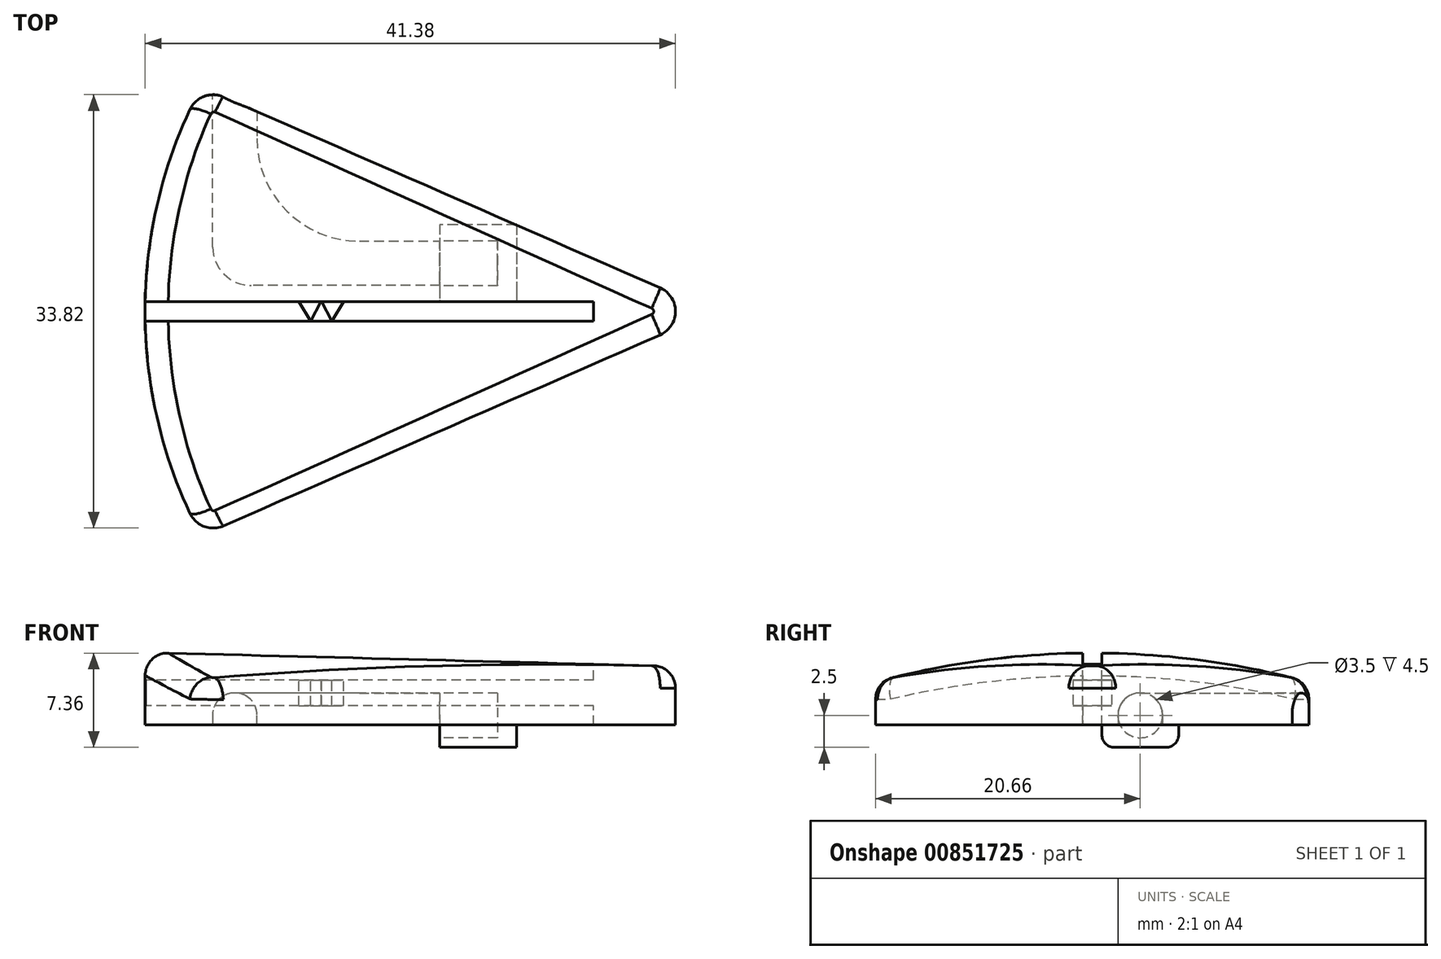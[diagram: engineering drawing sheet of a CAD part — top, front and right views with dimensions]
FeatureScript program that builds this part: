
annotation { "Feature Type Name" : "Feature", "Feature Type Description" : "" }
export const myFeature = defineFeature(function(context is Context, id is Id, definition is map)
    precondition{}
    {
        {
            var Q0;
            Q0=qCreatedBy(makeId("Top.planeOp"),FACE);
            var sketch = newSketch(context, id + "F0", { "sketchPlane" : qUnion([Q0])});
            skLineSegment(sketch, "E0", {"start": v(0, 0) * mm, "end": v(-40, 17.5) * mm, "construction": true});
            skLineSegment(sketch, "E1", {"start": v(-40, 17.5) * mm, "end": v(-40, -17.5) * mm, "construction": true});
            skLineSegment(sketch, "E2", {"start": v(-40, -17.5) * mm, "end": v(0, 0) * mm, "construction": true});
            skLineSegment(sketch, "E3", {"start": v(-4.19, 1.83) * mm, "end": v(-38.26, 16.74) * mm});
            skLineSegment(sketch, "E4", {"start": v(-38.26, -16.74) * mm, "end": v(-4.19, -1.83) * mm});
            skPoint(sketch, "E5.visualSharp", {"position": v(0, 0) * mm});
            skArc(sketch, "E5.filletArc", {"start": v(-4.19, -1.83) * mm, "mid": v(-2.99, 0) * mm, "end": v(-4.19, 1.83) * mm});
            skArc(sketch, "E6", {"start": v(-40.87, 15.75) * mm, "mid": v(-44.37, 0) * mm, "end": v(-40.87, -15.75) * mm});
            skPoint(sketch, "E7.visualSharp", {"position": v(-40, 17.5) * mm});
            skArc(sketch, "E7.filletArc", {"start": v(-38.26, 16.74) * mm, "mid": v(-39.77, 16.78) * mm, "end": v(-40.87, 15.75) * mm});
            skPoint(sketch, "E8.visualSharp", {"position": v(-40, -17.5) * mm});
            skArc(sketch, "E8.filletArc", {"start": v(-40.87, -15.75) * mm, "mid": v(-39.77, -16.78) * mm, "end": v(-38.26, -16.74) * mm});
            skSolve(sketch);
        }
        {
            var Q0;
            Q0 = qSketchRegion(id + "F0", true);
            extrude(context, id + "F1", {"entities" : qUnion([Q0]), "depth" : 6 * mm, "offsetDistance" : 25 * mm});
        }
        {
            var Q0;
            Q0=makeQuery(id+"F1.opExtrude","CAP_FACE",FACE,{"disambiguationData":[OSD([sQuery(id+"F0.wireOp",EDGE,"E3"),sQuery(id+"F0.wireOp",EDGE,"E4"),sQuery(id+"F0.wireOp",EDGE,"E5.filletArc"),sQuery(id+"F0.wireOp",EDGE,"E6"),sQuery(id+"F0.wireOp",EDGE,"E7.filletArc"),sQuery(id+"F0.wireOp",EDGE,"E8.filletArc")])],"isStart":false});
            var sketch = newSketch(context, id + "F2", { "sketchPlane" : qUnion([Q0])});
            skLineSegment(sketch, "E9.bottom", {"start": v(-9.37, 0.75) * mm, "end": v(-44.37, 0.75) * mm});
            skLineSegment(sketch, "E9.top", {"start": v(-9.37, -0.75) * mm, "end": v(-44.37, -0.75) * mm});
            skLineSegment(sketch, "E9.left", {"start": v(-9.37, 0.75) * mm, "end": v(-9.37, -0.75) * mm});
            skLineSegment(sketch, "E9.right", {"start": v(-44.37, 0.75) * mm, "end": v(-44.37, -0.75) * mm});
            skSolve(sketch);
        }
        {
            var Q0;
            Q0 = qSketchRegion(id + "F2", true);
            extrude(context, id + "F3", {"entities" : qUnion([Q0]), "operationType" : NewBodyOperationType.REMOVE, "endBound" : BoundingType.THROUGH_ALL, "oppositeDirection" : true, "depth" : 25 * mm, "offsetDistance" : 25 * mm});
        }
        {
            var Q0;
            Q0=qCreatedBy(makeId("Right.planeOp"),FACE);
            var sketch = newSketch(context, id + "F4", { "sketchPlane" : qUnion([Q0])});
            skLineSegment(sketch, "E10", {"start": v(-18, 2) * mm, "end": v(-18, 0) * mm, "construction": true});
            skLineSegment(sketch, "E11", {"start": v(-18, 0) * mm, "end": v(18, 0) * mm, "construction": true});
            skLineSegment(sketch, "E12", {"start": v(18, 0) * mm, "end": v(18, 2) * mm, "construction": true});
            skArc(sketch, "E13", {"start": v(18, 2) * mm, "mid": v(0, 4.5) * mm, "end": v(-18, 2) * mm});
            skLineSegment(sketch, "E14", {"start": v(-18, 2) * mm, "end": v(-18, 12) * mm});
            skLineSegment(sketch, "E15", {"start": v(-18, 12) * mm, "end": v(18, 12) * mm});
            skLineSegment(sketch, "E16", {"start": v(18, 12) * mm, "end": v(18, 2) * mm});
            skSolve(sketch);
        }
        {
            var Q0;
            Q0 = qSketchRegion(id + "F4", true);
            extrude(context, id + "F5", {"entities" : qUnion([Q0]), "operationType" : NewBodyOperationType.REMOVE, "endBound" : BoundingType.THROUGH_ALL, "oppositeDirection" : true, "depth" : 25 * mm, "offsetDistance" : 25 * mm, "hasDraft" : true, "draftAngle" : 1.5 * degree, "draftPullDirection" : true});
        }
        {
            var Q0;
            {var subQ0=sQuery(id+"F0.wireOp",EDGE,"E8.filletArc");var subQ2=sQuery(id+"F0.wireOp",EDGE,"E6");Q0=makeQuery(id+"F5.boolean.opBoolean","INTERSECT",EDGE,{"derivedFrom":[makeQuery(id+"F3.boolean.opBoolean","SPLIT",FACE,{"disambiguationData":[TD([makeQuery(id+"F1.opExtrude","SWEPT_FACE",FACE,{"disambiguationData":[OSD([subQ0])]})])],"derivedFrom":makeQuery(id+"F1.opExtrude","SWEPT_FACE",FACE,{"disambiguationData":[OSD([subQ2])]})}),makeQuery(id+"F5.opExtrude","SWEPT_FACE",FACE,{"disambiguationData":[OSD([sQuery(id+"F4.wireOp",EDGE,"E13")])]})]});}
            fillet(context, id + "F6", {"entities" : qUnion([Q0]), "radius" : 1.75 * mm, "tangentPropagation" : true, "allowEdgeOverflow" : false});
        }
        {
            var Q0;
            Q0=makeQuery(id+"F1.opExtrude","CAP_FACE",FACE,{"disambiguationData":[OSD([sQuery(id+"F0.wireOp",EDGE,"E3"),sQuery(id+"F0.wireOp",EDGE,"E4"),sQuery(id+"F0.wireOp",EDGE,"E5.filletArc"),sQuery(id+"F0.wireOp",EDGE,"E6"),sQuery(id+"F0.wireOp",EDGE,"E7.filletArc"),sQuery(id+"F0.wireOp",EDGE,"E8.filletArc")])],"isStart":true});
            var sketch = newSketch(context, id + "F7", { "sketchPlane" : qUnion([Q0])});
            skLineSegment(sketch, "E17.bottom", {"start": v(-15.37, -6.75) * mm, "end": v(-21.37, -6.75) * mm});
            skLineSegment(sketch, "E17.top", {"start": v(-15.37, -0.75) * mm, "end": v(-21.37, -0.75) * mm});
            skLineSegment(sketch, "E17.left", {"start": v(-15.37, -6.75) * mm, "end": v(-15.37, -0.75) * mm});
            skLineSegment(sketch, "E17.right", {"start": v(-21.37, -6.75) * mm, "end": v(-21.37, -0.75) * mm});
            skLineSegment(sketch, "E18", {"start": v(-44.18, -3.75) * mm, "end": v(-8.57, -3.75) * mm, "construction": true});
            skPoint(sketch, "E19", {"position": v(-21.37, -3.75) * mm});
            skSolve(sketch);
        }
        {
            var Q0;
            Q0 = qSketchRegion(id + "F7", true);
            extrude(context, id + "F8", {"entities" : qUnion([Q0]), "operationType" : NewBodyOperationType.ADD, "depth" : 1.75 * mm, "offsetDistance" : 25 * mm});
        }
        {
            var Q0;
            Q0=makeQuery(id+"F1.opExtrude","CAP_FACE",FACE,{"disambiguationData":[OSD([sQuery(id+"F0.wireOp",EDGE,"E3"),sQuery(id+"F0.wireOp",EDGE,"E4"),sQuery(id+"F0.wireOp",EDGE,"E5.filletArc"),sQuery(id+"F0.wireOp",EDGE,"E6"),sQuery(id+"F0.wireOp",EDGE,"E7.filletArc"),sQuery(id+"F0.wireOp",EDGE,"E8.filletArc")])],"isStart":true});
            var sketch = newSketch(context, id + "F9", { "sketchPlane" : qUnion([Q0])});
            skLineSegment(sketch, "E20", {"start": v(-21.37, -3.75) * mm, "end": v(-37.37, -3.75) * mm, "construction": true});
            skLineSegment(sketch, "E21", {"start": v(-37.37, -3.75) * mm, "end": v(-37.37, -18.75) * mm, "construction": true});
            skLineSegment(sketch, "E22", {"start": v(-21.37, -2.03) * mm, "end": v(-36.1, -2.03) * mm});
            skLineSegment(sketch, "E23", {"start": v(-39.1, -5.03) * mm, "end": v(-39.1, -18.75) * mm});
            skLineSegment(sketch, "E24", {"start": v(-39.1, -18.75) * mm, "end": v(-35.65, -18.75) * mm});
            skLineSegment(sketch, "E25", {"start": v(-35.65, -18.75) * mm, "end": v(-35.65, -13.48) * mm});
            skLineSegment(sketch, "E26", {"start": v(-27.65, -5.48) * mm, "end": v(-21.37, -5.48) * mm});
            skLineSegment(sketch, "E27", {"start": v(-29.37, -3.75) * mm, "end": v(-29.37, -2.03) * mm, "construction": true});
            skLineSegment(sketch, "E28", {"start": v(-29.37, -3.75) * mm, "end": v(-29.37, -5.48) * mm, "construction": true});
            skLineSegment(sketch, "E29", {"start": v(-37.37, -11.25) * mm, "end": v(-39.1, -11.25) * mm, "construction": true});
            skLineSegment(sketch, "E30", {"start": v(-37.37, -11.25) * mm, "end": v(-35.65, -11.25) * mm, "construction": true});
            skPoint(sketch, "E31.visualSharp", {"position": v(-39.1, -2.03) * mm});
            skArc(sketch, "E31.filletArc", {"start": v(-36.1, -2.03) * mm, "mid": v(-38.22, -2.9) * mm, "end": v(-39.1, -5.03) * mm});
            skPoint(sketch, "E32.visualSharp", {"position": v(-35.65, -5.48) * mm});
            skArc(sketch, "E32.filletArc", {"start": v(-27.65, -5.48) * mm, "mid": v(-33.3, -7.82) * mm, "end": v(-35.65, -13.48) * mm});
            skLineSegment(sketch, "E33", {"start": v(-21.37, -2.03) * mm, "end": v(-21.37, -5.48) * mm});
            skSolve(sketch);
        }
        {
            var Q0;
            Q0 = qSketchRegion(id + "F9", true);
            extrude(context, id + "F10", {"entities" : qUnion([Q0]), "operationType" : NewBodyOperationType.REMOVE, "oppositeDirection" : true, "depth" : 2.5 * mm, "offsetDistance" : 25 * mm});
        }
        {
            var Q0;
            Q0=makeQuery(id+"F10.boolean.opBoolean","COPY",EDGE,{"derivedFrom":makeQuery(id+"F10.opExtrude","CAP_EDGE",EDGE,{"disambiguationData":[OSD([sQuery(id+"F9.wireOp",EDGE,"E32.filletArc")])],"isStart":false})});
            var Q1;
            Q1=makeQuery(id+"F10.boolean.opBoolean","COPY",EDGE,{"derivedFrom":makeQuery(id+"F10.opExtrude","CAP_EDGE",EDGE,{"disambiguationData":[OSD([sQuery(id+"F9.wireOp",EDGE,"E23")])],"isStart":false})});
            fillet(context, id + "F11", {"entities" : qUnion([Q0, Q1]), "radius" : 1.7 * mm, "tangentPropagation" : true, "allowEdgeOverflow" : false});
        }
        {
            var Q0;
            Q0=makeQuery(id+"F10.boolean.opBoolean","MERGE",FACE,{"derivedFrom":[makeQuery(id+"F8.opExtrude","SWEPT_FACE",FACE,{"disambiguationData":[OSD([sQuery(id+"F7.wireOp",EDGE,"E17.right")])]})],"fromTools":[makeQuery(id+"F10.opExtrude","SWEPT_FACE",FACE,{"disambiguationData":[OSD([sQuery(id+"F9.wireOp",EDGE,"E33")])]})]});
            var sketch = newSketch(context, id + "F12", { "sketchPlane" : qUnion([Q0])});
            skCircle(sketch, "E34", {"center": v(-3.75, 0.75) * mm, "radius": 1.75 * mm});
            skPoint(sketch, "E34.centerSnap0", {"position": v(-3.75, 2.5) * mm});
            skSolve(sketch);
        }
        {
            var Q0;
            Q0 = qSketchRegion(id + "F12", true);
            extrude(context, id + "F13", {"entities" : qUnion([Q0]), "operationType" : NewBodyOperationType.REMOVE, "oppositeDirection" : true, "depth" : 4.5 * mm, "offsetDistance" : 25 * mm});
        }
        {
            var Q0;
            Q0=makeQuery(id+"F8.opExtrude","CAP_EDGE",EDGE,{"disambiguationData":[OSD([sQuery(id+"F7.wireOp",EDGE,"E17.top")])],"isStart":false});
            var Q1;
            Q1=makeQuery(id+"F8.opExtrude","CAP_EDGE",EDGE,{"disambiguationData":[OSD([sQuery(id+"F7.wireOp",EDGE,"E17.bottom")])],"isStart":false});
            fillet(context, id + "F14", {"entities" : qUnion([Q0, Q1]), "radius" : 1 * mm, "tangentPropagation" : true, "allowEdgeOverflow" : false});
        }
        {
            var Q0;
            {var subQ0=sQuery(id+"F0.wireOp",EDGE,"E7.filletArc");var subQ1=sQuery(id+"F0.wireOp",EDGE,"E6");Q0=makeQuery(id+"F10.boolean.opBoolean","SPLIT",FACE,{"disambiguationData":[TD([makeQuery(id+"F1.opExtrude","SWEPT_FACE",FACE,{"disambiguationData":[OSD([subQ0])]})])],"derivedFrom":makeQuery(id+"F1.opExtrude","CAP_FACE",FACE,{"disambiguationData":[OSD([sQuery(id+"F0.wireOp",EDGE,"E3"),sQuery(id+"F0.wireOp",EDGE,"E4"),sQuery(id+"F0.wireOp",EDGE,"E5.filletArc"),subQ1,subQ0,sQuery(id+"F0.wireOp",EDGE,"E8.filletArc")])],"isStart":true})});}
            cPlane(context, id + "F15", {"entities" : qUnion([Q0]), "cplaneType" : CPlaneType.OFFSET, "offset" : 2.5 * mm, "oppositeDirection" : true, "width" : 150 * mm, "height" : 150 * mm});
        }
        {
            var Q0;
            Q0=qCreatedBy(id+"F15.planeOp",FACE);
            var sketch = newSketch(context, id + "F16", { "sketchPlane" : qUnion([Q0])});
            skLineSegment(sketch, "E35.bottom", {"start": v(-44.37, 0.75) * mm, "end": v(-9.37, 0.75) * mm, "construction": true});
            skLineSegment(sketch, "E35.left", {"start": v(-44.37, 0.75) * mm, "end": v(-44.37, -0.75) * mm, "construction": true});
            skLineSegment(sketch, "E35.right", {"start": v(-9.37, 0.75) * mm, "end": v(-9.37, -0.75) * mm, "construction": true});
            skLineSegment(sketch, "E36.bottom", {"start": v(-44.37, -1.5) * mm, "end": v(-9.37, -1.5) * mm});
            skLineSegment(sketch, "E36.top", {"start": v(-44.37, 1.5) * mm, "end": v(-9.37, 1.5) * mm});
            skLineSegment(sketch, "E36.left", {"start": v(-44.37, -1.5) * mm, "end": v(-44.37, 1.5) * mm});
            skLineSegment(sketch, "E36.right", {"start": v(-9.37, -1.5) * mm, "end": v(-9.37, 1.5) * mm});
            skLineSegment(sketch, "E37", {"start": v(-32.37, -0.75) * mm, "end": v(-31.45, 0.75) * mm});
            skLineSegment(sketch, "E38", {"start": v(-31.45, 0.75) * mm, "end": v(-30.62, -0.8) * mm});
            skLineSegment(sketch, "E39", {"start": v(-30.62, -0.8) * mm, "end": v(-29.79, 0.75) * mm});
            skLineSegment(sketch, "E40", {"start": v(-29.79, 0.75) * mm, "end": v(-28.87, -0.75) * mm});
            skPoint(sketch, "E41", {"position": v(-9.37, 0) * mm});
            skLineSegment(sketch, "E42", {"start": v(-32.37, -0.75) * mm, "end": v(-32.37, -1.2) * mm});
            skLineSegment(sketch, "E43", {"start": v(-32.37, -1.2) * mm, "end": v(-30.62, -1.2) * mm});
            skLineSegment(sketch, "E44", {"start": v(-30.62, -1.2) * mm, "end": v(-28.88, -1.2) * mm});
            skLineSegment(sketch, "E45", {"start": v(-28.88, -1.2) * mm, "end": v(-28.87, -0.75) * mm});
            skSolve(sketch);
        }
        {
            var Q0;
            Q0 = qSketchRegion(id + "F16", true);
            extrude(context, id + "F17", {"entities" : qUnion([Q0]), "operationType" : NewBodyOperationType.ADD, "depth" : 1 * mm, "offsetDistance" : 25 * mm, "hasSecondDirection" : true, "secondDirectionOppositeDirection" : true, "secondDirectionDepth" : 1 * mm});
        }
    });
